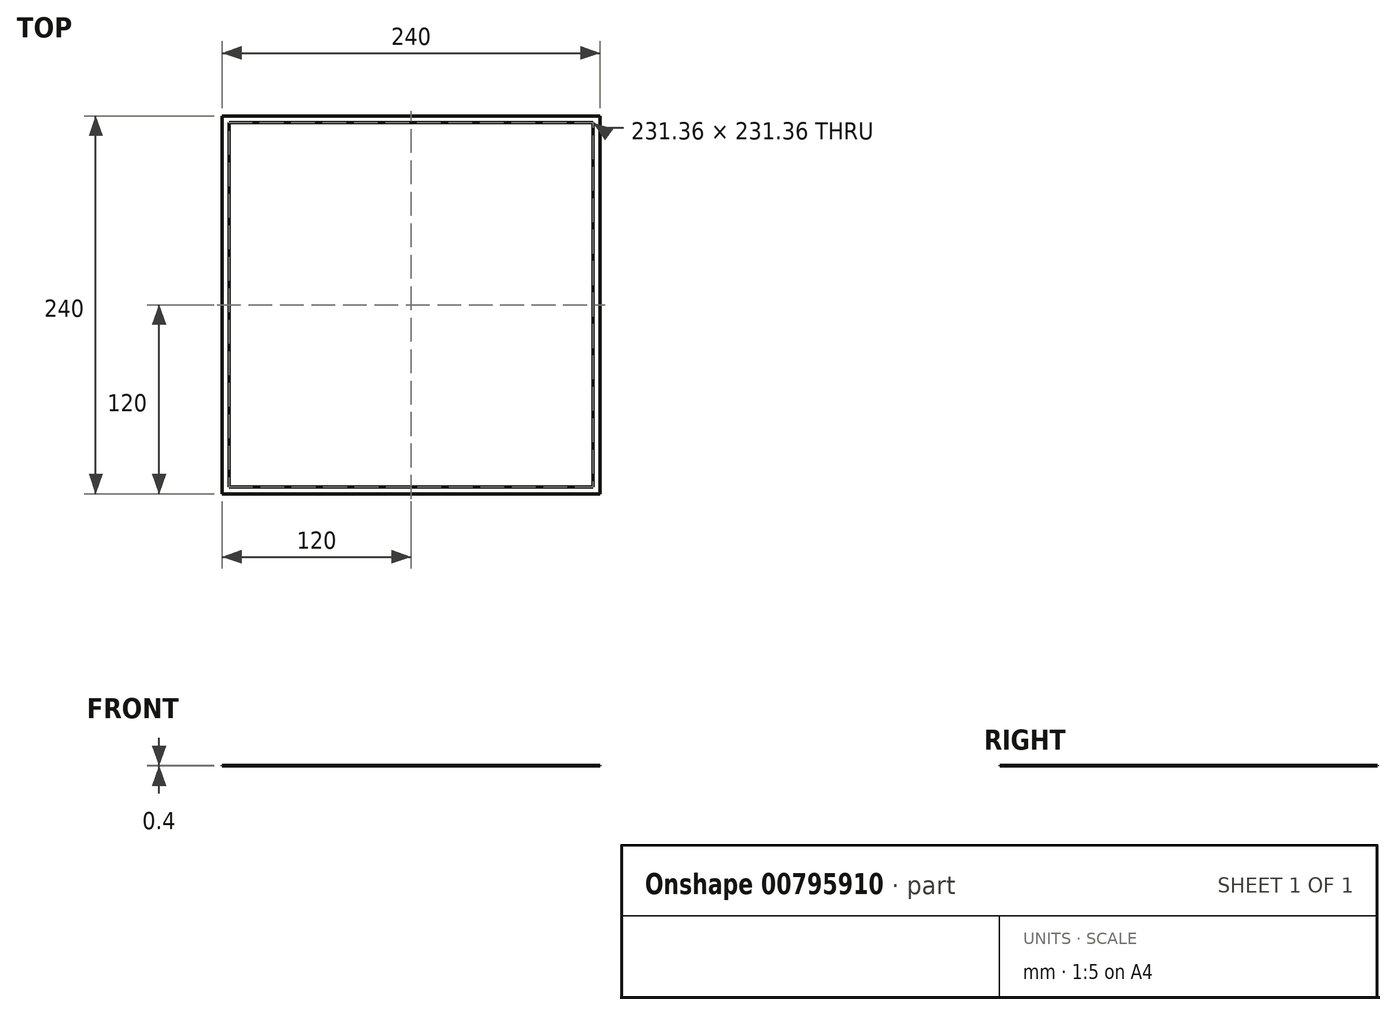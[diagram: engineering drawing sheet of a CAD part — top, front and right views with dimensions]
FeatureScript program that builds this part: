
annotation { "Feature Type Name" : "Feature", "Feature Type Description" : "" }
export const myFeature = defineFeature(function(context is Context, id is Id, definition is map)
    precondition{}
    {
        {
            var Q0;
            Q0=qCreatedBy(makeId("Top.planeOp"),FACE);
            var sketch = newSketch(context, id + "F0", { "sketchPlane" : qUnion([Q0])});
            skLineSegment(sketch, "E0.bottom", {"start": v(120, 120) * mm, "end": v(-120, 120) * mm});
            skLineSegment(sketch, "E0.top", {"start": v(120, -120) * mm, "end": v(-120, -120) * mm});
            skLineSegment(sketch, "E0.left", {"start": v(120, 120) * mm, "end": v(120, -120) * mm});
            skLineSegment(sketch, "E0.right", {"start": v(-120, 120) * mm, "end": v(-120, -120) * mm});
            skPoint(sketch, "E0.middle", {"position": v(0, 0) * mm});
            skLineSegment(sketch, "E1.0", {"start": v(115.68, 115.68) * mm, "end": v(-115.68, 115.68) * mm});
            skLineSegment(sketch, "E1.1", {"start": v(115.68, 115.68) * mm, "end": v(115.68, -115.68) * mm});
            skLineSegment(sketch, "E1.2", {"start": v(115.68, -115.68) * mm, "end": v(-115.68, -115.68) * mm});
            skLineSegment(sketch, "E1.3", {"start": v(-115.68, 115.68) * mm, "end": v(-115.68, -115.68) * mm});
            skSolve(sketch);
        }
        {
            var Q0;
            Q0=makeQuery(id+"F0.imprint","IMPRINT",FACE,{"disambiguationData":[TD([[makeQuery(id+"F0.imprint","IMPRINT",EDGE,{"derivedFrom":sQuery(id+"F0.wireOp",EDGE,"E0.bottom")}),1.0]])]});
            extrude(context, id + "F1", {"entities" : qUnion([Q0]), "depth" : 0.4 * mm, "offsetDistance" : 25.4 * mm});
        }
    });
